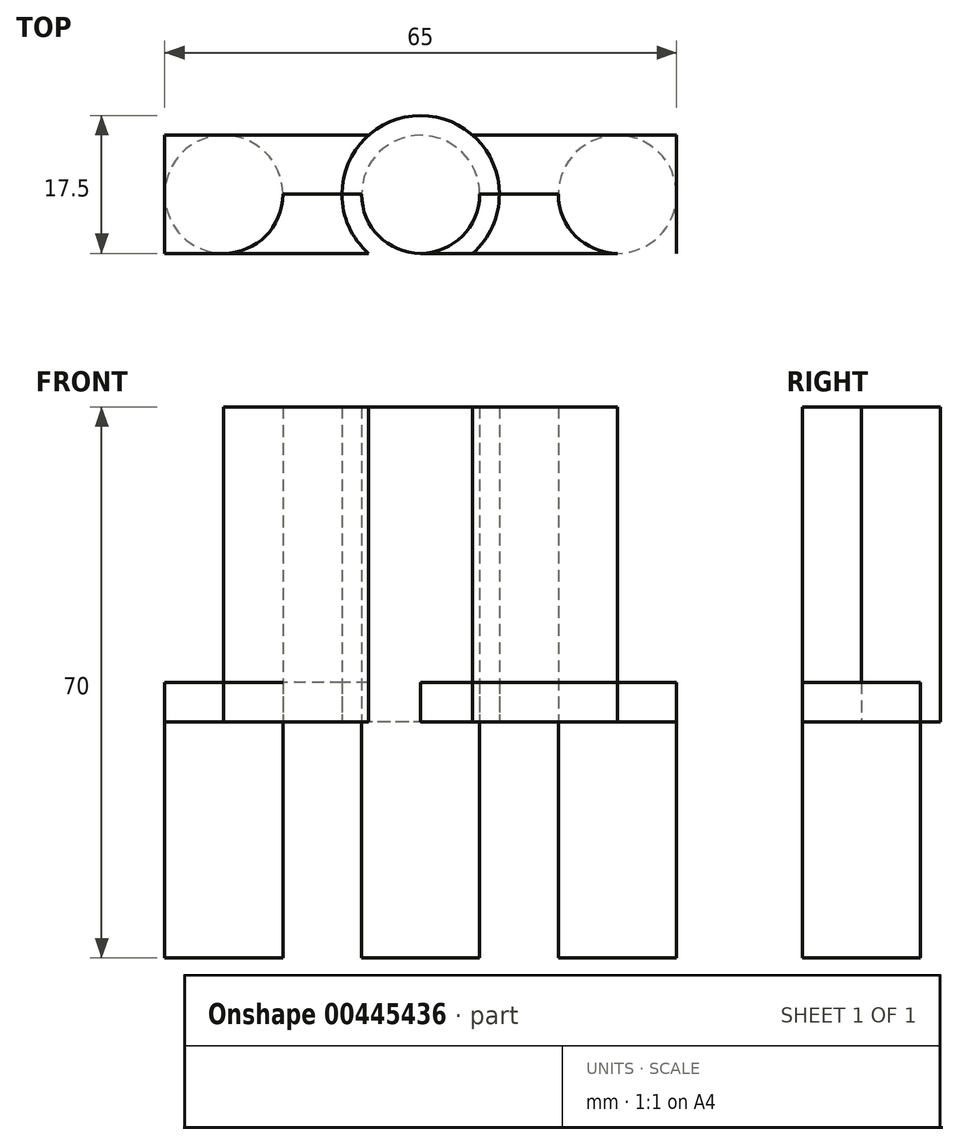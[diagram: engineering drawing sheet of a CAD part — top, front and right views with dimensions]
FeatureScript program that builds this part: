
annotation { "Feature Type Name" : "Feature", "Feature Type Description" : "" }
export const myFeature = defineFeature(function(context is Context, id is Id, definition is map)
    precondition{}
    {
        {
            var Q0;
            Q0=qCreatedBy(makeId("Top.planeOp"),FACE);
            var sketch = newSketch(context, id + "F0", { "sketchPlane" : qUnion([Q0])});
            skLineSegment(sketch, "E0.bottom", {"start": v(32.5, -7.5) * mm, "end": v(-32.5, -7.5) * mm});
            skLineSegment(sketch, "E0.top", {"start": v(32.5, 7.5) * mm, "end": v(-32.5, 7.5) * mm});
            skLineSegment(sketch, "E0.left", {"start": v(32.5, -7.5) * mm, "end": v(32.5, 7.5) * mm});
            skLineSegment(sketch, "E0.right", {"start": v(-32.5, -7.5) * mm, "end": v(-32.5, 7.5) * mm});
            skPoint(sketch, "E0.middle", {"position": v(0, 0) * mm});
            skCircle(sketch, "E1", {"center": v(0, 0) * mm, "radius": 10 * mm});
            skCircle(sketch, "E2", {"center": v(0, 0) * mm, "radius": 7.5 * mm});
            skLineSegment(sketch, "E3", {"start": v(-7.5, 0) * mm, "end": v(-25, 0) * mm});
            skCircle(sketch, "E4", {"center": v(-25, 0) * mm, "radius": 7.5 * mm});
            skLineSegment(sketch, "E5", {"start": v(7.5, 0) * mm, "end": v(25, 0) * mm});
            skCircle(sketch, "E6", {"center": v(25, 0) * mm, "radius": 7.5 * mm});
            skSolve(sketch);
        }
        {
            var Q0;
            {var subQ0=sQuery(id+"F0.wireOp",EDGE,"E4");var subQ1=makeQuery(id+"F0.imprint","INTERSECT",VERTEX,{"derivedFrom":[sQuery(id+"F0.wireOp",EDGE,"E0.top"),subQ0]});Q0=makeQuery(id+"F0.imprint","IMPRINT",FACE,{"disambiguationData":[TD([[makeQuery(id+"F0.imprint","IMPRINT",EDGE,{"disambiguationData":[TD([[subQ1,1.0]])],"derivedFrom":subQ0}),1.0]])]});}
            var Q1;
            {var subQ0=sQuery(id+"F0.wireOp",EDGE,"E2");var subQ1=makeQuery(id+"F0.imprint","INTERSECT",VERTEX,{"derivedFrom":[subQ0,sQuery(id+"F0.wireOp",EDGE,"E5")]});Q1=makeQuery(id+"F0.imprint","IMPRINT",FACE,{"disambiguationData":[TD([[makeQuery(id+"F0.imprint","IMPRINT",EDGE,{"disambiguationData":[TD([[subQ1,-1.0]])],"derivedFrom":subQ0}),1.0]])]});}
            var Q2;
            {var subQ0=sQuery(id+"F0.wireOp",EDGE,"E6");var subQ1=makeQuery(id+"F0.imprint","INTERSECT",VERTEX,{"derivedFrom":[sQuery(id+"F0.wireOp",EDGE,"E0.top"),subQ0]});Q2=makeQuery(id+"F0.imprint","IMPRINT",FACE,{"disambiguationData":[TD([[makeQuery(id+"F0.imprint","IMPRINT",EDGE,{"disambiguationData":[TD([[subQ1,1.0]])],"derivedFrom":subQ0}),1.0]])]});}
            extrude(context, id + "F1", {"entities" : qUnion([Q0, Q1, Q2]), "oppositeDirection" : true, "depth" : 30 * mm});
        }
        {
            var Q0;
            {var subQ0=sQuery(id+"F0.wireOp",EDGE,"E1");var subQ1=sQuery(id+"F0.wireOp",EDGE,"E0.top");var subQ2=makeQuery(id+"F0.imprint","INTERSECT",VERTEX,{"disambiguationData":[OD(0.0)],"derivedFrom":[subQ1,subQ0]});Q0=makeQuery(id+"F0.imprint","IMPRINT",FACE,{"disambiguationData":[TD([[makeQuery(id+"F0.imprint","IMPRINT",EDGE,{"disambiguationData":[TD([[subQ2,-1.0]])],"derivedFrom":subQ1}),1.0]])]});}
            var Q1;
            {var subQ0=sQuery(id+"F0.wireOp",EDGE,"E1");var subQ1=sQuery(id+"F0.wireOp",EDGE,"E0.top");var subQ2=makeQuery(id+"F0.imprint","INTERSECT",VERTEX,{"disambiguationData":[OD(0.0)],"derivedFrom":[subQ1,subQ0]});Q1=makeQuery(id+"F0.imprint","IMPRINT",FACE,{"disambiguationData":[TD([[makeQuery(id+"F0.imprint","IMPRINT",EDGE,{"disambiguationData":[TD([[subQ2,-1.0]])],"derivedFrom":subQ1}),-1.0]])]});}
            var Q2;
            {var subQ0=sQuery(id+"F0.wireOp",EDGE,"E1");var subQ1=sQuery(id+"F0.wireOp",EDGE,"E0.top");var subQ2=makeQuery(id+"F0.imprint","INTERSECT",VERTEX,{"disambiguationData":[OD(1.0)],"derivedFrom":[subQ1,subQ0]});Q2=makeQuery(id+"F0.imprint","IMPRINT",FACE,{"disambiguationData":[TD([[makeQuery(id+"F0.imprint","IMPRINT",EDGE,{"disambiguationData":[TD([[subQ2,1.0]])],"derivedFrom":subQ1}),1.0]])]});}
            var Q3;
            {var subQ0=sQuery(id+"F0.wireOp",EDGE,"E2");var subQ1=makeQuery(id+"F0.imprint","INTERSECT",VERTEX,{"derivedFrom":[subQ0,sQuery(id+"F0.wireOp",EDGE,"E5")]});Q3=makeQuery(id+"F0.imprint","IMPRINT",FACE,{"disambiguationData":[TD([[makeQuery(id+"F0.imprint","IMPRINT",EDGE,{"disambiguationData":[TD([[subQ1,-1.0]])],"derivedFrom":subQ0}),1.0]])]});}
            var Q4;
            {var subQ0=sQuery(id+"F0.wireOp",EDGE,"E1");var subQ1=sQuery(id+"F0.wireOp",EDGE,"E0.bottom");var subQ2=makeQuery(id+"F0.imprint","INTERSECT",VERTEX,{"disambiguationData":[OD(0.0)],"derivedFrom":[subQ1,subQ0]});Q4=makeQuery(id+"F0.imprint","IMPRINT",FACE,{"disambiguationData":[TD([[makeQuery(id+"F0.imprint","IMPRINT",EDGE,{"disambiguationData":[TD([[subQ2,-1.0]])],"derivedFrom":subQ1}),-1.0]])]});}
            var Q5;
            {var subQ0=sQuery(id+"F0.wireOp",EDGE,"E1");var subQ1=sQuery(id+"F0.wireOp",EDGE,"E0.bottom");var subQ2=makeQuery(id+"F0.imprint","INTERSECT",VERTEX,{"disambiguationData":[OD(0.0)],"derivedFrom":[subQ1,subQ0]});Q5=makeQuery(id+"F0.imprint","IMPRINT",FACE,{"disambiguationData":[TD([[makeQuery(id+"F0.imprint","IMPRINT",EDGE,{"disambiguationData":[TD([[subQ2,-1.0]])],"derivedFrom":subQ1}),1.0]])]});}
            var Q6;
            {var subQ0=sQuery(id+"F0.wireOp",EDGE,"E1");var subQ1=sQuery(id+"F0.wireOp",EDGE,"E0.bottom");var subQ2=makeQuery(id+"F0.imprint","INTERSECT",VERTEX,{"disambiguationData":[OD(1.0)],"derivedFrom":[subQ1,subQ0]});Q6=makeQuery(id+"F0.imprint","IMPRINT",FACE,{"disambiguationData":[TD([[makeQuery(id+"F0.imprint","IMPRINT",EDGE,{"disambiguationData":[TD([[subQ2,1.0]])],"derivedFrom":subQ1}),-1.0]])]});}
            extrude(context, id + "F2", {"entities" : qUnion([Q0, Q1, Q2, Q3, Q4, Q5, Q6]), "operationType" : NewBodyOperationType.ADD, "depth" : 40 * mm});
        }
        {
            var Q0;
            {var subQ0=sQuery(id+"F0.wireOp",EDGE,"E0.right");var subQ1=sQuery(id+"F0.wireOp",EDGE,"E0.top");var subQ2=makeQuery(id+"F0.imprint","INTERSECT",VERTEX,{"derivedFrom":[subQ1,subQ0]});Q0=makeQuery(id+"F0.imprint","IMPRINT",FACE,{"disambiguationData":[TD([[makeQuery(id+"F0.imprint","IMPRINT",EDGE,{"disambiguationData":[TD([[subQ2,1.0]])],"derivedFrom":subQ1}),1.0]])]});}
            var Q1;
            {var subQ0=sQuery(id+"F0.wireOp",EDGE,"E0.right");var subQ1=sQuery(id+"F0.wireOp",EDGE,"E0.bottom");var subQ2=makeQuery(id+"F0.imprint","INTERSECT",VERTEX,{"derivedFrom":[subQ1,subQ0]});Q1=makeQuery(id+"F0.imprint","IMPRINT",FACE,{"disambiguationData":[TD([[makeQuery(id+"F0.imprint","IMPRINT",EDGE,{"disambiguationData":[TD([[subQ2,1.0]])],"derivedFrom":subQ1}),-1.0]])]});}
            var Q2;
            {var subQ0=sQuery(id+"F0.wireOp",EDGE,"E1");var subQ1=sQuery(id+"F0.wireOp",EDGE,"E0.bottom");var subQ2=makeQuery(id+"F0.imprint","INTERSECT",VERTEX,{"disambiguationData":[OD(1.0)],"derivedFrom":[subQ1,subQ0]});Q2=makeQuery(id+"F0.imprint","IMPRINT",FACE,{"disambiguationData":[TD([[makeQuery(id+"F0.imprint","IMPRINT",EDGE,{"disambiguationData":[TD([[subQ2,-1.0]])],"derivedFrom":subQ1}),-1.0]])]});}
            var Q3;
            {var subQ0=sQuery(id+"F0.wireOp",EDGE,"E6");var subQ1=sQuery(id+"F0.wireOp",EDGE,"E0.top");var subQ2=makeQuery(id+"F0.imprint","INTERSECT",VERTEX,{"derivedFrom":[subQ1,subQ0]});Q3=makeQuery(id+"F0.imprint","IMPRINT",FACE,{"disambiguationData":[TD([[makeQuery(id+"F0.imprint","IMPRINT",EDGE,{"disambiguationData":[TD([[subQ2,-1.0]])],"derivedFrom":subQ1}),1.0]])]});}
            var Q4;
            {var subQ0=sQuery(id+"F0.wireOp",EDGE,"E6");var subQ1=sQuery(id+"F0.wireOp",EDGE,"E0.bottom");var subQ2=makeQuery(id+"F0.imprint","INTERSECT",VERTEX,{"derivedFrom":[subQ1,subQ0]});Q4=makeQuery(id+"F0.imprint","IMPRINT",FACE,{"disambiguationData":[TD([[makeQuery(id+"F0.imprint","IMPRINT",EDGE,{"disambiguationData":[TD([[subQ2,-1.0]])],"derivedFrom":subQ1}),-1.0]])]});}
            var Q5;
            {var subQ0=sQuery(id+"F0.wireOp",EDGE,"E1");var subQ1=sQuery(id+"F0.wireOp",EDGE,"E0.top");var subQ2=makeQuery(id+"F0.imprint","INTERSECT",VERTEX,{"disambiguationData":[OD(1.0)],"derivedFrom":[subQ1,subQ0]});Q5=makeQuery(id+"F0.imprint","IMPRINT",FACE,{"disambiguationData":[TD([[makeQuery(id+"F0.imprint","IMPRINT",EDGE,{"disambiguationData":[TD([[subQ2,-1.0]])],"derivedFrom":subQ1}),1.0]])]});}
            var Q6;
            {var subQ0=sQuery(id+"F0.wireOp",EDGE,"E0.left");var subQ1=sQuery(id+"F0.wireOp",EDGE,"E0.bottom");var subQ2=makeQuery(id+"F0.imprint","INTERSECT",VERTEX,{"derivedFrom":[subQ1,subQ0]});Q6=makeQuery(id+"F0.imprint","IMPRINT",FACE,{"disambiguationData":[TD([[makeQuery(id+"F0.imprint","IMPRINT",EDGE,{"disambiguationData":[TD([[subQ2,-1.0]])],"derivedFrom":subQ1}),-1.0]])]});}
            var Q7;
            {var subQ0=sQuery(id+"F0.wireOp",EDGE,"E0.left");var subQ1=sQuery(id+"F0.wireOp",EDGE,"E0.top");var subQ2=makeQuery(id+"F0.imprint","INTERSECT",VERTEX,{"derivedFrom":[subQ1,subQ0]});Q7=makeQuery(id+"F0.imprint","IMPRINT",FACE,{"disambiguationData":[TD([[makeQuery(id+"F0.imprint","IMPRINT",EDGE,{"disambiguationData":[TD([[subQ2,-1.0]])],"derivedFrom":subQ1}),1.0]])]});}
            var Q8;
            {var subQ0=sQuery(id+"F0.wireOp",EDGE,"E6");var subQ1=makeQuery(id+"F0.imprint","INTERSECT",VERTEX,{"derivedFrom":[sQuery(id+"F0.wireOp",EDGE,"E0.top"),subQ0]});Q8=makeQuery(id+"F0.imprint","IMPRINT",FACE,{"disambiguationData":[TD([[makeQuery(id+"F0.imprint","IMPRINT",EDGE,{"disambiguationData":[TD([[subQ1,1.0]])],"derivedFrom":subQ0}),1.0]])]});}
            var Q9;
            {var subQ0=sQuery(id+"F0.wireOp",EDGE,"E4");var subQ1=makeQuery(id+"F0.imprint","INTERSECT",VERTEX,{"derivedFrom":[sQuery(id+"F0.wireOp",EDGE,"E0.top"),subQ0]});Q9=makeQuery(id+"F0.imprint","IMPRINT",FACE,{"disambiguationData":[TD([[makeQuery(id+"F0.imprint","IMPRINT",EDGE,{"disambiguationData":[TD([[subQ1,1.0]])],"derivedFrom":subQ0}),1.0]])]});}
            extrude(context, id + "F3", {"entities" : qUnion([Q0, Q1, Q2, Q3, Q4, Q5, Q6, Q7, Q8, Q9]), "depth" : 5 * mm});
        }
    });
